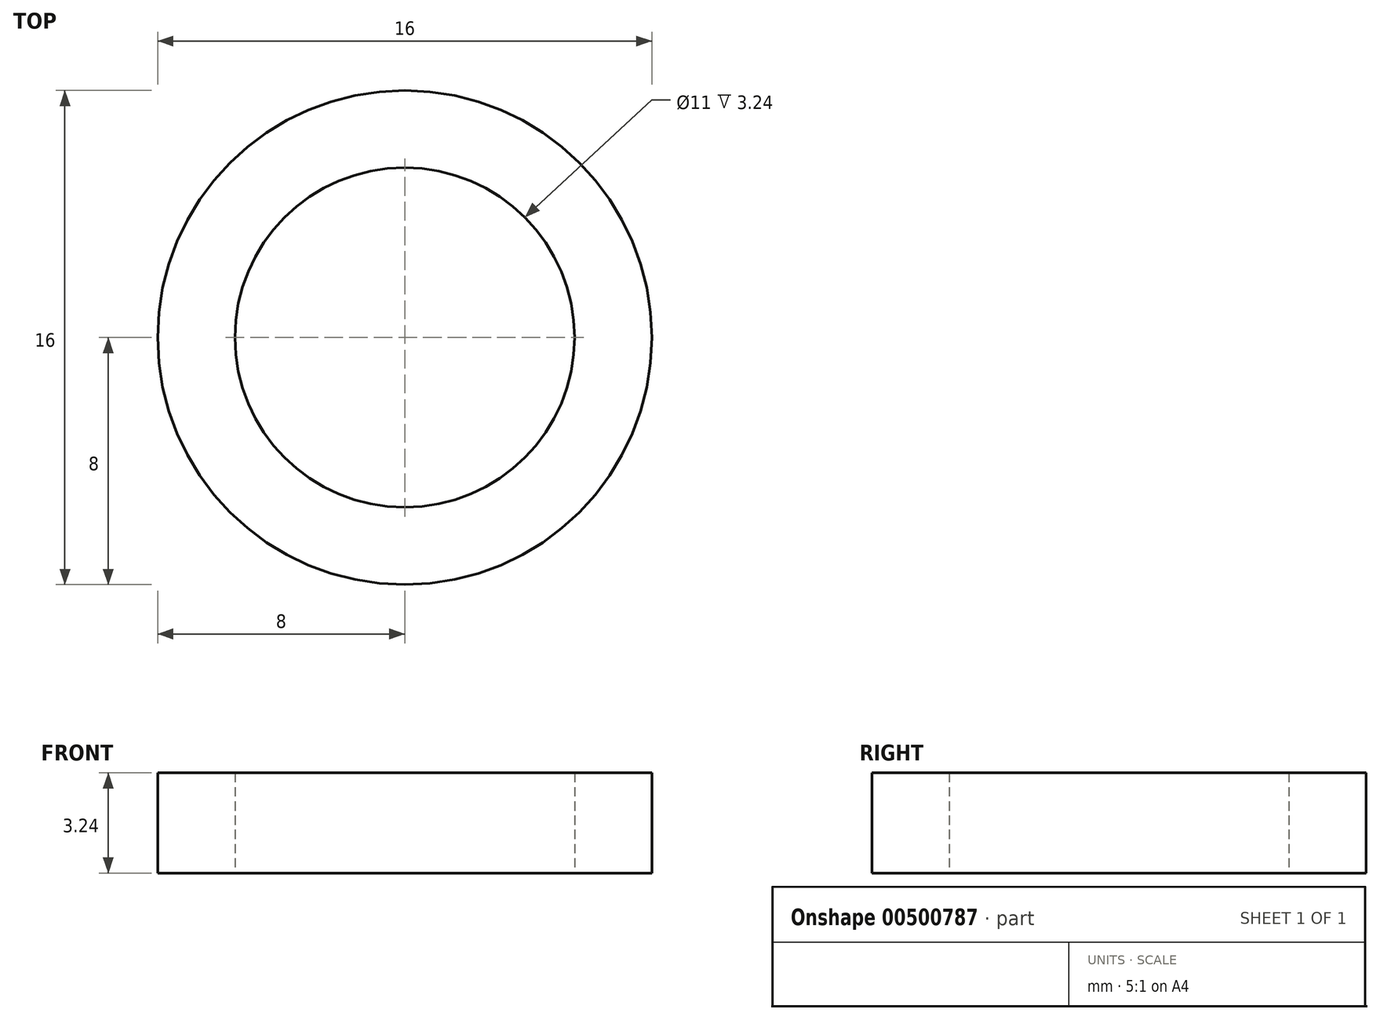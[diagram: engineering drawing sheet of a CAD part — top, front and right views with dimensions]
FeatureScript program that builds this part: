
annotation { "Feature Type Name" : "Feature", "Feature Type Description" : "" }
export const myFeature = defineFeature(function(context is Context, id is Id, definition is map)
    precondition{}
    {
        {
            var Q0;
            Q0=qCreatedBy(makeId("Top.planeOp"),FACE);
            var sketch = newSketch(context, id + "F0", { "sketchPlane" : qUnion([Q0])});
            skCircle(sketch, "E0", {"center": v(0, 0) * mm, "radius": 5.5 * mm});
            skCircle(sketch, "E1", {"center": v(0, 0) * mm, "radius": 8 * mm});
            skSolve(sketch);
        }
        {
            var Q0;
            Q0=makeQuery(id+"F0.imprint","IMPRINT",FACE,{"disambiguationData":[TD([[makeQuery(id+"F0.imprint","IMPRINT",EDGE,{"derivedFrom":sQuery(id+"F0.wireOp",EDGE,"E0")}),-1.0]])]});
            extrude(context, id + "F1", {"entities" : qUnion([Q0]), "depth" : 3.24 * mm, "offsetDistance" : 25 * mm});
        }
    });
